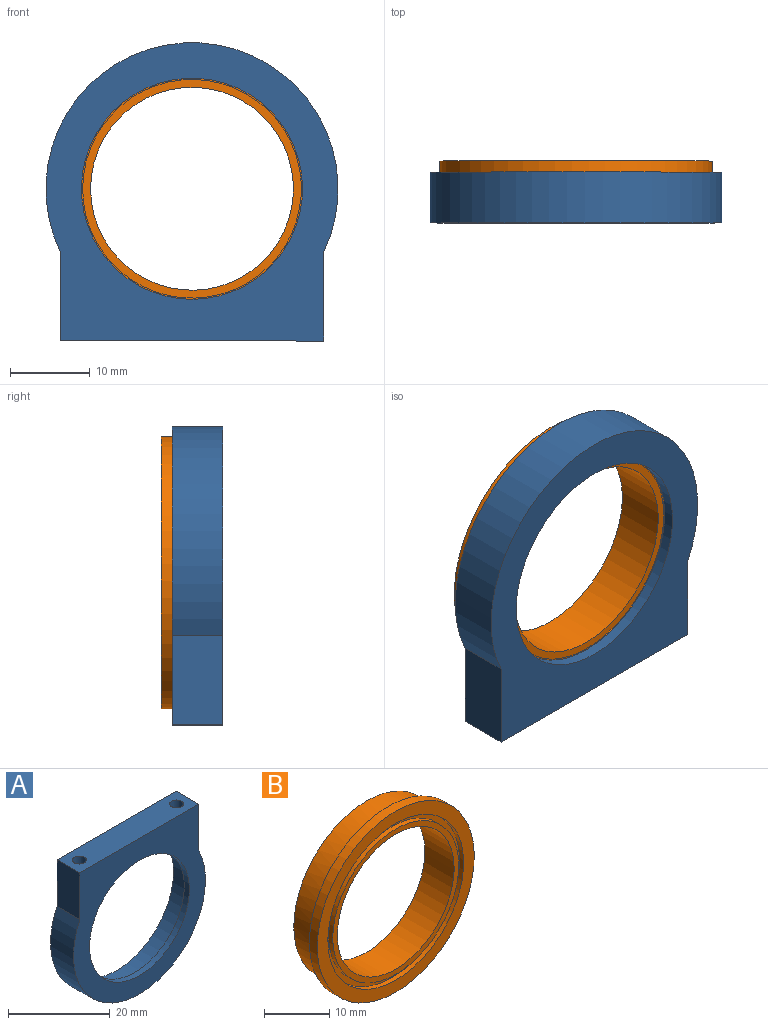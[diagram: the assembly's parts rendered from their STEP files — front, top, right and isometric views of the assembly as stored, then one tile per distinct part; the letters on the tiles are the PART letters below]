
ASSEMBLY  parts=2 mates=1
PART A: 13 faces, bbox 36.6x6.4x37.3 mm
  f0: cylinder r=1.35mm len=7.62mm, axis (0,0,1), area 64.8mm2, adj f1,f7
  f1: cone r=1.35mm half-angle=59deg, axis (0,0,1), area 6.7mm2, adj f0
  f2: cylinder r=1.35mm len=7.62mm, axis (0,0,1), area 64.8mm2, adj f3,f7
  f3: cone r=1.35mm half-angle=59deg, axis (0,0,1), area 6.7mm2, adj f2
  f4: cylinder r=13.84mm len=27.69mm, axis (0,1,0), area 121.5mm2, adj f11,f12
  f5: cylinder r=15.81mm len=31.62mm, axis (0,1,0), area 492.1mm2, adj f10,f12
  f6: cylinder r=18.29mm len=36.58mm, axis (0,-1,0), area 468.1mm2, adj f8,f9,f10,f11
  f7: plane 33.02x6.35mm, normal (0,0,1), area 198.2mm2, adj f0,f2,f8,f9,f10,f11
  f8: plane 11.18x6.35mm, normal (1,0,0), area 71mm2, adj f6,f7,f10,f11
  f9: plane 11.18x6.35mm, normal (-1,0,0), area 71mm2, adj f6,f7,f10,f11
  f10: plane 37.34x36.58mm, normal (0,1,0), area 387.8mm2, adj f5,f6,f7,f8,f9
  f11: plane 37.34x36.58mm, normal (0,-1,0), area 571.2mm2, adj f4,f6,f7,f8,f9
  f12: plane 31.62x31.62mm, normal (0,1,0), area 183.4mm2, adj f4,f5
PART B: 14 faces, bbox 34.1x6.4x34.1 mm
  f0: cylinder r=17.06mm len=34.13mm, axis (0,-1,0), area 183.8mm2, adj f10,f13
  f1: cylinder r=13.69mm len=27.38mm, axis (0,-1,0), area 76.5mm2, adj f7,f12
  f2: cylinder r=14.76mm len=29.52mm, axis (0,-1,0), area 82.4mm2, adj f10,f12
  f3: cylinder r=13.69mm len=27.38mm, axis (0,1,0), area 76.5mm2, adj f8,f11
  f4: cylinder r=14.76mm len=29.52mm, axis (0,1,0), area 82.4mm2, adj f9,f11
  f5: cylinder r=12.7mm len=25.4mm, axis (0,-1,0), area 506.7mm2, adj f7,f8
  f6: cylinder r=15.81mm len=31.62mm, axis (0,-1,0), area 460.5mm2, adj f9,f13
  f7: plane 27.38x27.38mm, normal (0,-1,0), area 82.1mm2, adj f1,f5
  f8: plane 27.38x27.38mm, normal (0,1,0), area 82.1mm2, adj f3,f5
  f9: plane 31.62x31.62mm, normal (0,1,0), area 101.2mm2, adj f4,f6
  f10: plane 34.13x34.13mm, normal (0,-1,0), area 230.4mm2, adj f0,f2
  f11: plane 29.52x29.52mm, normal (0,1,0), area 95.3mm2, adj f3,f4
  f12: plane 29.52x29.52mm, normal (0,-1,0), area 95.3mm2, adj f1,f2
  f13: plane 34.13x34.13mm, normal (0,1,0), area 129.2mm2, adj f0,f6
PLACE A rot(axis=(0,-1,0),180deg) t=(0.79,45.26,18.78)mm
PLACE B rot(axis=(-0.71,0,0.71),180deg) t=(0.79,53.01,18.78)mm
MATE fastened A.f4 <-> B.f0  axis (0,1,0) through (0.79,46.66,18.78)mm
